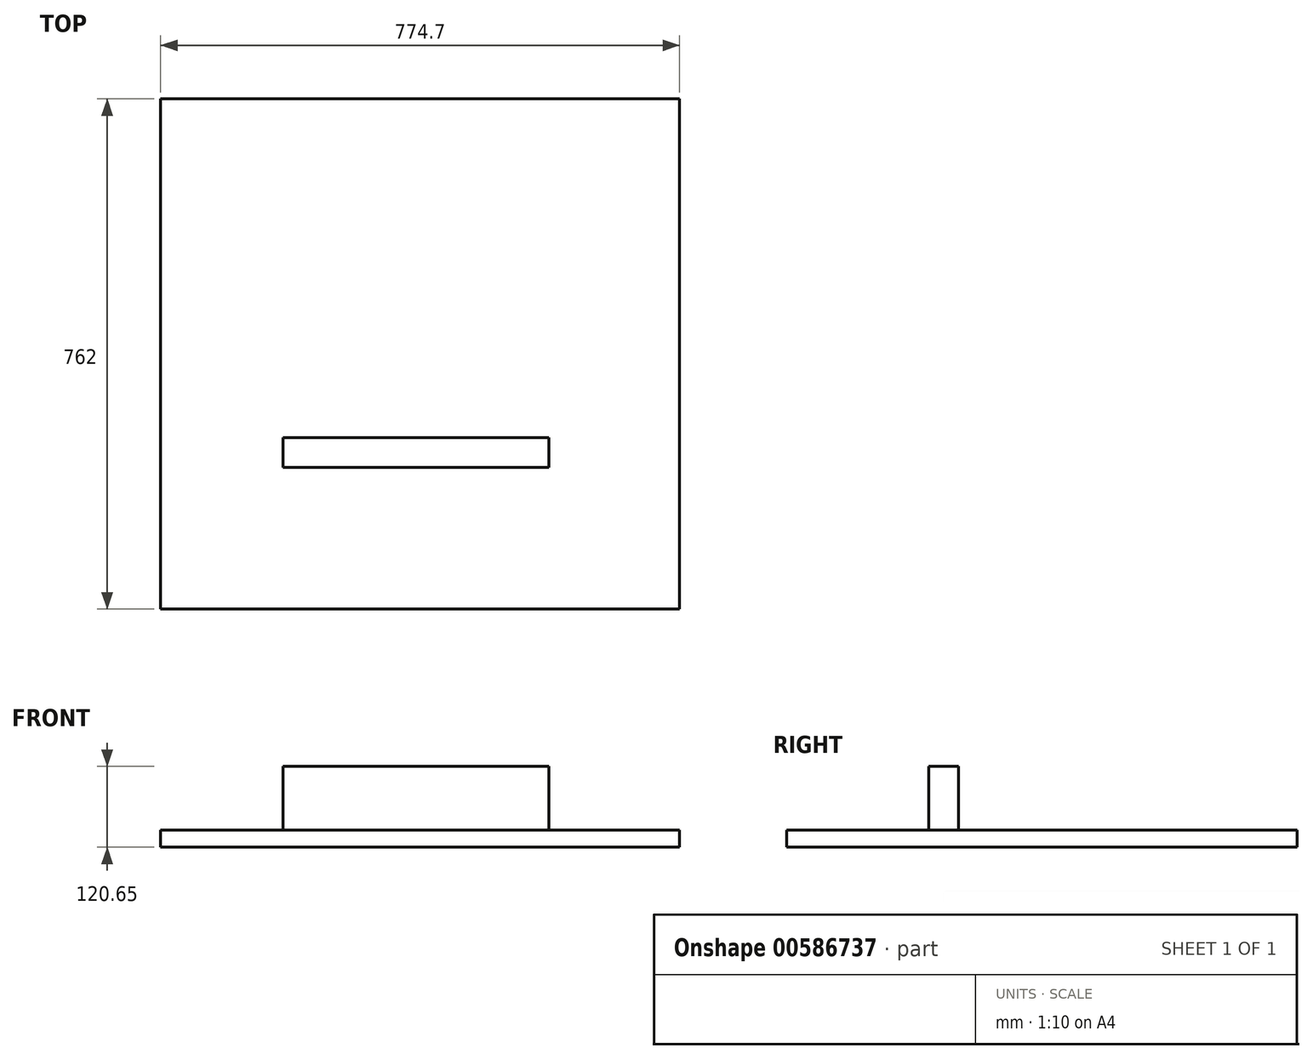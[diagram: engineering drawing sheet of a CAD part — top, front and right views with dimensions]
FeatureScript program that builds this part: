
annotation { "Feature Type Name" : "Feature", "Feature Type Description" : "" }
export const myFeature = defineFeature(function(context is Context, id is Id, definition is map)
    precondition{}
    {
        {
            var Q0;
            Q0=qCreatedBy(makeId("Top.planeOp"),FACE);
            var sketch = newSketch(context, id + "F0", { "sketchPlane" : qUnion([Q0])});
            skLineSegment(sketch, "E0.bottom", {"start": v(381, 381) * mm, "end": v(-381, 381) * mm});
            skLineSegment(sketch, "E0.top", {"start": v(381, -381) * mm, "end": v(-381, -381) * mm});
            skLineSegment(sketch, "E0.left", {"start": v(381, 381) * mm, "end": v(381, -381) * mm});
            skLineSegment(sketch, "E0.right", {"start": v(-381, 381) * mm, "end": v(-381, -381) * mm});
            skPoint(sketch, "E0.middle", {"position": v(0, 0) * mm});
            skSolve(sketch);
        }
        {
            var Q0;
            Q0=makeQuery(id+"F0.imprint","IMPRINT",FACE,{"disambiguationData":[TD([[makeQuery(id+"F0.imprint","IMPRINT",EDGE,{"derivedFrom":sQuery(id+"F0.wireOp",EDGE,"E0.bottom")}),1.0]])]});
            extrude(context, id + "F1", {"entities" : qUnion([Q0]), "depth" : 25.4 * mm, "offsetDistance" : 25.4 * mm});
        }
        {
            var Q0;
            Q0=makeQuery(id+"F1.opExtrude","SWEPT_FACE",FACE,{"disambiguationData":[OSD([sQuery(id+"F0.wireOp",EDGE,"E0.left")])]});
            extrude(context, id + "F2", {"entities" : qUnion([Q0]), "operationType" : NewBodyOperationType.ADD, "depth" : 12.7 * mm, "offsetDistance" : 25.4 * mm});
        }
        {
            var Q0;
            {var subQ0=sQuery(id+"F0.wireOp",EDGE,"E0.left");Q0=makeQuery(id+"F2.boolean.opBoolean","MERGE",FACE,{"derivedFrom":[makeQuery(id+"F1.opExtrude","CAP_FACE",FACE,{"disambiguationData":[OSD([sQuery(id+"F0.wireOp",EDGE,"E0.bottom"),sQuery(id+"F0.wireOp",EDGE,"E0.top"),subQ0,sQuery(id+"F0.wireOp",EDGE,"E0.right")])],"isStart":false}),makeQuery(id+"F2.opExtrude","SWEPT_FACE",FACE,{"disambiguationData":[OSD([subQ0]),TDD([makeQuery(id+"F1.opExtrude","CAP_EDGE",EDGE,{"disambiguationData":[OSD([subQ0])],"isStart":false})])]})]});}
            var sketch = newSketch(context, id + "F3", { "sketchPlane" : qUnion([Q0])});
            skLineSegment(sketch, "E1.bottom", {"start": v(-304.8, -99.52) * mm, "end": v(304.8, -99.52) * mm});
            skLineSegment(sketch, "E1.top", {"start": v(-304.8, -143.97) * mm, "end": v(304.8, -143.97) * mm});
            skLineSegment(sketch, "E1.left", {"start": v(-304.8, -99.52) * mm, "end": v(-304.8, -143.97) * mm});
            skLineSegment(sketch, "E1.right", {"start": v(304.8, -99.52) * mm, "end": v(304.8, -143.97) * mm});
            skPoint(sketch, "E1.middle", {"position": v(0, -121.74) * mm});
            skSolve(sketch);
        }
        {
            var Q0;
            {var subQ0=sQuery(id+"F0.wireOp",EDGE,"E0.left");Q0=makeQuery(id+"F2.boolean.opBoolean","MERGE",FACE,{"derivedFrom":[makeQuery(id+"F1.opExtrude","CAP_FACE",FACE,{"disambiguationData":[OSD([sQuery(id+"F0.wireOp",EDGE,"E0.bottom"),sQuery(id+"F0.wireOp",EDGE,"E0.top"),subQ0,sQuery(id+"F0.wireOp",EDGE,"E0.right")])],"isStart":false}),makeQuery(id+"F2.opExtrude","SWEPT_FACE",FACE,{"disambiguationData":[OSD([subQ0]),TDD([makeQuery(id+"F1.opExtrude","CAP_EDGE",EDGE,{"disambiguationData":[OSD([subQ0])],"isStart":false})])]})]});}
            var sketch = newSketch(context, id + "F4", { "sketchPlane" : qUnion([Q0])});
            skLineSegment(sketch, "E2.bottom", {"start": v(-198.57, -124.7) * mm, "end": v(198.57, -124.7) * mm});
            skLineSegment(sketch, "E2.top", {"start": v(-198.57, -169.15) * mm, "end": v(198.57, -169.15) * mm});
            skLineSegment(sketch, "E2.left", {"start": v(-198.57, -124.7) * mm, "end": v(-198.57, -169.15) * mm});
            skLineSegment(sketch, "E2.right", {"start": v(198.57, -124.7) * mm, "end": v(198.57, -169.15) * mm});
            skPoint(sketch, "E2.middle", {"position": v(0, -146.92) * mm});
            skSolve(sketch);
        }
        {
            var Q0;
            Q0=makeQuery(id+"F4.imprint","IMPRINT",FACE,{"disambiguationData":[TD([[makeQuery(id+"F4.imprint","IMPRINT",EDGE,{"derivedFrom":sQuery(id+"F4.wireOp",EDGE,"E2.bottom")}),-1.0]])]});
            extrude(context, id + "F5", {"entities" : qUnion([Q0]), "operationType" : NewBodyOperationType.ADD, "depth" : 95.25 * mm, "offsetDistance" : 25.4 * mm});
        }
    });
